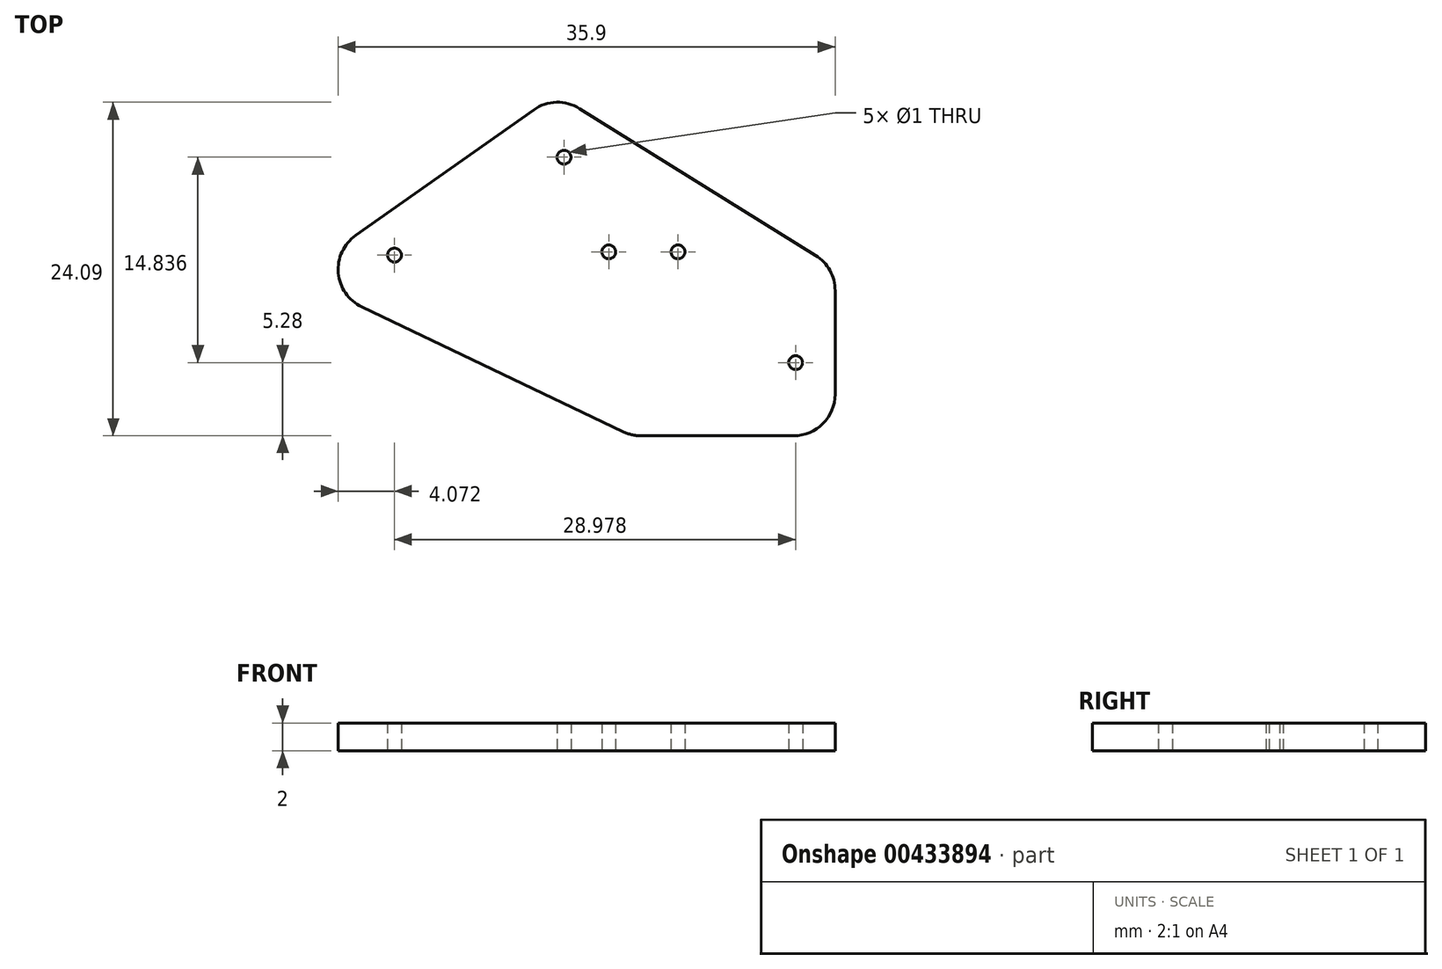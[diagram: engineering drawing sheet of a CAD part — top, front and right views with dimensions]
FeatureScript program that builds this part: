
annotation { "Feature Type Name" : "Feature", "Feature Type Description" : "" }
export const myFeature = defineFeature(function(context is Context, id is Id, definition is map)
    precondition{}
    {
        {
            var Q0;
            Q0=qCreatedBy(makeId("Top.planeOp"),FACE);
            var sketch = newSketch(context, id + "F0", { "sketchPlane" : qUnion([Q0])});
            skCircle(sketch, "E0", {"center": v(0, 0) * mm, "radius": 0.5 * mm});
            skCircle(sketch, "E1", {"center": v(-28.98, 7.76) * mm, "radius": 0.5 * mm});
            skCircle(sketch, "E2", {"center": v(-16.73, 14.84) * mm, "radius": 0.5 * mm});
            skLineSegment(sketch, "E3", {"start": v(0, 0) * mm, "end": v(-28.98, 7.76) * mm, "construction": true});
            skPoint(sketch, "E4", {"position": v(-19.32, 5.18) * mm});
            skLineSegment(sketch, "E5", {"start": v(-16.73, 14.84) * mm, "end": v(-19.32, 5.18) * mm, "construction": true});
            skLineSegment(sketch, "E6", {"start": v(2.85, -5.28) * mm, "end": v(-11.86, -5.28) * mm});
            skLineSegment(sketch, "E7", {"start": v(-17.3, 19.4) * mm, "end": v(-35.96, 6.24) * mm});
            skLineSegment(sketch, "E8", {"start": v(-17.3, 19.4) * mm, "end": v(2.85, 6.87) * mm});
            skLineSegment(sketch, "E9", {"start": v(2.85, 6.87) * mm, "end": v(2.85, -5.28) * mm});
            skLineSegment(sketch, "E10", {"start": v(-11.86, -5.28) * mm, "end": v(-35.96, 6.24) * mm});
            skPoint(sketch, "E11", {"position": v(-8.5, 8) * mm});
            skPoint(sketch, "E12", {"position": v(-13.5, 8) * mm});
            skLineSegment(sketch, "E13", {"start": v(-13.5, 8) * mm, "end": v(-8.5, 8) * mm, "construction": true});
            skCircle(sketch, "E14", {"center": v(-13.5, 8) * mm, "radius": 0.5 * mm});
            skCircle(sketch, "E15", {"center": v(-8.5, 8) * mm, "radius": 0.5 * mm});
            skSolve(sketch);
        }
        {
            var Q0;
            Q0=makeQuery(id+"F0.imprint","IMPRINT",FACE,{"disambiguationData":[TD([[makeQuery(id+"F0.imprint","IMPRINT",EDGE,{"derivedFrom":sQuery(id+"F0.wireOp",EDGE,"E0")}),-1.0]])]});
            extrude(context, id + "F1", {"entities" : qUnion([Q0]), "depth" : 2 * mm});
        }
        {
            var Q0;
            Q0=makeQuery(id+"F1.opExtrude","SWEPT_EDGE",EDGE,{"disambiguationData":[OSD([sQuery(id+"F0.wireOp",EDGE,"d5Qg5dhI-nyps-Npmx-gZQv-n4vqtGnI5Wim"),sQuery(id+"F0.wireOp",EDGE,"E7")])]});
            var Q1;
            Q1=makeQuery(id+"F1.opExtrude","SWEPT_EDGE",EDGE,{"disambiguationData":[OSD([sQuery(id+"F0.wireOp",EDGE,"E7"),sQuery(id+"F0.wireOp",EDGE,"E8")])]});
            var Q2;
            Q2=makeQuery(id+"F1.opExtrude","SWEPT_EDGE",EDGE,{"disambiguationData":[OSD([sQuery(id+"F0.wireOp",EDGE,"E6"),sQuery(id+"F0.wireOp",EDGE,"d5Qg5dhI-nyps-Npmx-gZQv-n4vqtGnI5Wim")])]});
            var Q3;
            Q3=makeQuery(id+"F1.opExtrude","SWEPT_EDGE",EDGE,{"disambiguationData":[OSD([sQuery(id+"F0.wireOp",EDGE,"E6"),sQuery(id+"F0.wireOp",EDGE,"E9")])]});
            var Q4;
            Q4=makeQuery(id+"F1.opExtrude","SWEPT_EDGE",EDGE,{"disambiguationData":[OSD([sQuery(id+"F0.wireOp",EDGE,"E8"),sQuery(id+"F0.wireOp",EDGE,"E9")])]});
            fillet(context, id + "F2", {"entities" : qUnion([Q0, Q1, Q2, Q3, Q4]), "radius" : 3 * mm, "tangentPropagation" : true, "allowEdgeOverflow" : false});
        }
    });
